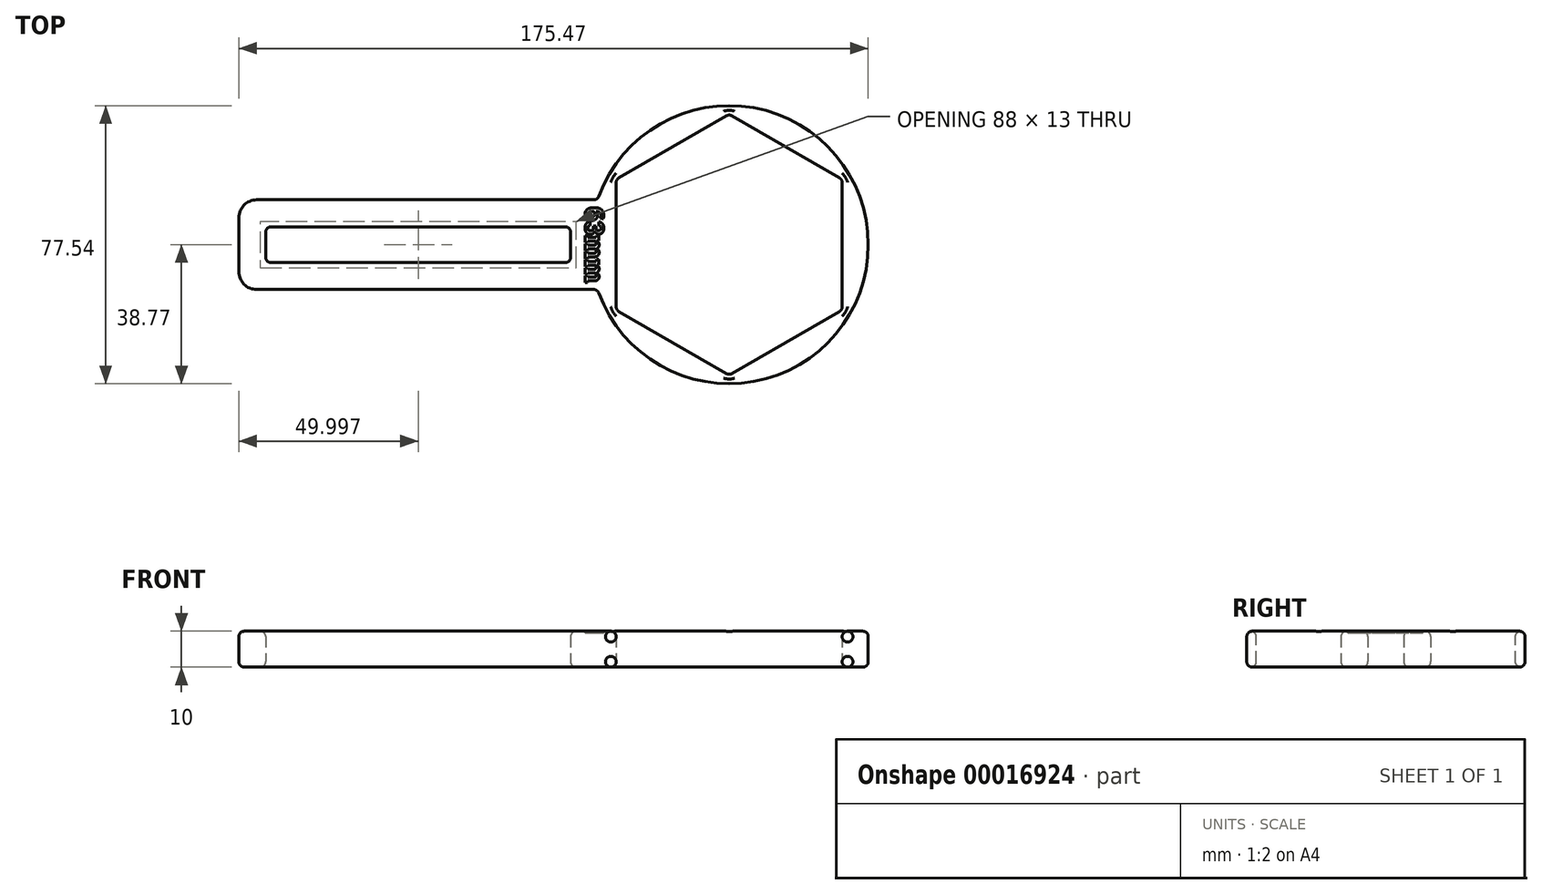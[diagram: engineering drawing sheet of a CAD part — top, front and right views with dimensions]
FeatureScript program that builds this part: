
annotation { "Feature Type Name" : "Feature", "Feature Type Description" : "" }
export const myFeature = defineFeature(function(context is Context, id is Id, definition is map)
    precondition{}
    {
        {
            var Q0;
            Q0=qCreatedBy(makeId("Top.planeOp"),FACE);
            var sketch = newSketch(context, id + "F0", { "sketchPlane" : qUnion([Q0])});
            skCircle(sketch, "E0.cCircle", {"center": v(0, 0) * mm, "radius": 31.5 * mm, "construction": true});
            skLineSegment(sketch, "E0.0", {"start": v(31.5, 18.19) * mm, "end": v(31.5, -18.19) * mm});
            skLineSegment(sketch, "E0.1", {"start": v(31.5, -18.19) * mm, "end": v(0, -36.37) * mm});
            skLineSegment(sketch, "E0.2", {"start": v(0, -36.37) * mm, "end": v(-31.5, -18.19) * mm});
            skLineSegment(sketch, "E0.3", {"start": v(-31.5, -18.19) * mm, "end": v(-31.5, 18.19) * mm});
            skLineSegment(sketch, "E0.4", {"start": v(-31.5, 18.19) * mm, "end": v(0, 36.37) * mm});
            skLineSegment(sketch, "E0.5", {"start": v(0, 36.37) * mm, "end": v(31.5, 18.19) * mm});
            skPoint(sketch, "E0.0.midPoint", {"position": v(31.5, 0) * mm});
            skArc(sketch, "E1", {"start": v(-36.7, -12.5) * mm, "mid": v(38.77, 0) * mm, "end": v(-36.7, 12.5) * mm});
            skLineSegment(sketch, "E2.rect.bottom", {"start": v(-36.7, 12.5) * mm, "end": v(-136.7, 12.5) * mm});
            skLineSegment(sketch, "E2.rect.top", {"start": v(-36.7, -12.5) * mm, "end": v(-136.7, -12.5) * mm});
            skLineSegment(sketch, "E2.rect.left", {"start": v(-31.5, 12.5) * mm, "end": v(-31.5, -12.5) * mm});
            skLineSegment(sketch, "E2.rect.right", {"start": v(-136.7, 12.5) * mm, "end": v(-136.7, -12.5) * mm});
            skPoint(sketch, "E2.rect.middle", {"position": v(-84.1, 0) * mm});
            skLineSegment(sketch, "E3.rect.bottom", {"start": v(-44.2, 5) * mm, "end": v(-129.2, 5) * mm});
            skLineSegment(sketch, "E3.rect.top", {"start": v(-44.2, -5) * mm, "end": v(-129.2, -5) * mm});
            skLineSegment(sketch, "E3.rect.left", {"start": v(-44.2, 5) * mm, "end": v(-44.2, -5) * mm});
            skLineSegment(sketch, "E3.rect.right", {"start": v(-129.2, 5) * mm, "end": v(-129.2, -5) * mm});
            skPoint(sketch, "E3.rect.middle", {"position": v(-86.7, 0) * mm});
            skSolve(sketch);
        }
        {
            var Q0;
            Q0=makeQuery(id+"F0.imprint","IMPRINT",FACE,{"disambiguationData":[TD([[makeQuery(id+"F0.imprint","IMPRINT",EDGE,{"derivedFrom":sQuery(id+"F0.wireOp",EDGE,"E0.0")}),1.0]])]});
            extrude(context, id + "F1", {"entities" : qUnion([Q0]), "depth" : 10 * mm});
        }
        {
            var Q0;
            Q0=makeQuery(id+"F1.opExtrude","CAP_EDGE",EDGE,{"disambiguationData":[OSD([sQuery(id+"F0.wireOp",EDGE,"E3.rect.right")])],"isStart":false});
            var Q1;
            Q1=makeQuery(id+"F1.opExtrude","CAP_EDGE",EDGE,{"disambiguationData":[OSD([sQuery(id+"F0.wireOp",EDGE,"E2.rect.right")])],"isStart":false});
            var Q2;
            Q2=makeQuery(id+"F1.opExtrude","SWEPT_EDGE",EDGE,{"disambiguationData":[OSD([sQuery(id+"F0.wireOp",EDGE,"E3.rect.bottom"),sQuery(id+"F0.wireOp",EDGE,"E3.rect.right")])]});
            var Q3;
            Q3=makeQuery(id+"F1.opExtrude","CAP_EDGE",EDGE,{"disambiguationData":[OSD([sQuery(id+"F0.wireOp",EDGE,"E2.rect.right")])],"isStart":true});
            var Q4;
            Q4=makeQuery(id+"F1.opExtrude","CAP_EDGE",EDGE,{"disambiguationData":[OSD([sQuery(id+"F0.wireOp",EDGE,"E3.rect.right")])],"isStart":true});
            var Q5;
            Q5=makeQuery(id+"F1.opExtrude","SWEPT_EDGE",EDGE,{"disambiguationData":[OSD([sQuery(id+"F0.wireOp",EDGE,"E3.rect.top"),sQuery(id+"F0.wireOp",EDGE,"E3.rect.right")])]});
            var Q6;
            Q6=makeQuery(id+"F1.opExtrude","CAP_EDGE",EDGE,{"disambiguationData":[OSD([sQuery(id+"F0.wireOp",EDGE,"E3.rect.bottom")])],"isStart":false});
            var Q7;
            Q7=makeQuery(id+"F1.opExtrude","CAP_EDGE",EDGE,{"disambiguationData":[OSD([sQuery(id+"F0.wireOp",EDGE,"E3.rect.bottom")])],"isStart":true});
            var Q8;
            Q8=makeQuery(id+"F1.opExtrude","CAP_EDGE",EDGE,{"disambiguationData":[OSD([sQuery(id+"F0.wireOp",EDGE,"E2.rect.top")])],"isStart":false});
            var Q9;
            Q9=makeQuery(id+"F1.opExtrude","CAP_EDGE",EDGE,{"disambiguationData":[OSD([sQuery(id+"F0.wireOp",EDGE,"E3.rect.top")])],"isStart":false});
            var Q10;
            Q10=makeQuery(id+"F1.opExtrude","CAP_EDGE",EDGE,{"disambiguationData":[OSD([sQuery(id+"F0.wireOp",EDGE,"E2.rect.top")])],"isStart":true});
            var Q11;
            Q11=makeQuery(id+"F1.opExtrude","CAP_EDGE",EDGE,{"disambiguationData":[OSD([sQuery(id+"F0.wireOp",EDGE,"E2.rect.bottom")])],"isStart":false});
            var Q12;
            Q12=makeQuery(id+"F1.opExtrude","CAP_EDGE",EDGE,{"disambiguationData":[OSD([sQuery(id+"F0.wireOp",EDGE,"E2.rect.bottom")])],"isStart":true});
            var Q13;
            Q13=makeQuery(id+"F1.opExtrude","CAP_EDGE",EDGE,{"disambiguationData":[OSD([sQuery(id+"F0.wireOp",EDGE,"E3.rect.top")])],"isStart":true});
            var Q14;
            Q14=makeQuery(id+"F1.opExtrude","CAP_EDGE",EDGE,{"disambiguationData":[OSD([sQuery(id+"F0.wireOp",EDGE,"E0.2")])],"isStart":false});
            var Q15;
            Q15=makeQuery(id+"F1.opExtrude","CAP_EDGE",EDGE,{"disambiguationData":[OSD([sQuery(id+"F0.wireOp",EDGE,"E1")])],"isStart":true});
            var Q16;
            Q16=makeQuery(id+"F1.opExtrude","CAP_EDGE",EDGE,{"disambiguationData":[OSD([sQuery(id+"F0.wireOp",EDGE,"E0.1")])],"isStart":false});
            var Q17;
            Q17=makeQuery(id+"F1.opExtrude","SWEPT_EDGE",EDGE,{"disambiguationData":[OSD([sQuery(id+"F0.wireOp",EDGE,"E1"),sQuery(id+"F0.wireOp",EDGE,"E2.rect.top")])]});
            var Q18;
            Q18=makeQuery(id+"F1.opExtrude","CAP_EDGE",EDGE,{"disambiguationData":[OSD([sQuery(id+"F0.wireOp",EDGE,"E0.0")])],"isStart":false});
            var Q19;
            Q19=makeQuery(id+"F1.opExtrude","CAP_EDGE",EDGE,{"disambiguationData":[OSD([sQuery(id+"F0.wireOp",EDGE,"E0.3"),sQuery(id+"F0.wireOp",EDGE,"E2.rect.left")])],"isStart":false});
            var Q20;
            Q20=makeQuery(id+"F1.opExtrude","CAP_EDGE",EDGE,{"disambiguationData":[OSD([sQuery(id+"F0.wireOp",EDGE,"E1")])],"isStart":false});
            var Q21;
            Q21=makeQuery(id+"F1.opExtrude","CAP_EDGE",EDGE,{"disambiguationData":[OSD([sQuery(id+"F0.wireOp",EDGE,"E0.2")])],"isStart":true});
            var Q22;
            Q22=makeQuery(id+"F1.opExtrude","CAP_EDGE",EDGE,{"disambiguationData":[OSD([sQuery(id+"F0.wireOp",EDGE,"E0.5")])],"isStart":false});
            var Q23;
            Q23=makeQuery(id+"F1.opExtrude","SWEPT_EDGE",EDGE,{"disambiguationData":[OSD([sQuery(id+"F0.wireOp",EDGE,"E3.rect.top"),sQuery(id+"F0.wireOp",EDGE,"E3.rect.left")])]});
            var Q24;
            Q24=makeQuery(id+"F1.opExtrude","SWEPT_EDGE",EDGE,{"disambiguationData":[OSD([sQuery(id+"F0.wireOp",EDGE,"E3.rect.bottom"),sQuery(id+"F0.wireOp",EDGE,"E3.rect.left")])]});
            var Q25;
            Q25=makeQuery(id+"F1.opExtrude","SWEPT_EDGE",EDGE,{"disambiguationData":[OSD([sQuery(id+"F0.wireOp",EDGE,"E1"),sQuery(id+"F0.wireOp",EDGE,"E2.rect.bottom")])]});
            var Q26;
            Q26=makeQuery(id+"F1.opExtrude","SWEPT_EDGE",EDGE,{"disambiguationData":[OSD([sQuery(id+"F0.wireOp",EDGE,"E0.4"),sQuery(id+"F0.wireOp",EDGE,"E0.5")])]});
            var Q27;
            Q27=makeQuery(id+"F1.opExtrude","SWEPT_EDGE",EDGE,{"disambiguationData":[OSD([sQuery(id+"F0.wireOp",EDGE,"E0.3"),sQuery(id+"F0.wireOp",EDGE,"E0.4")])]});
            var Q28;
            Q28=makeQuery(id+"F1.opExtrude","CAP_EDGE",EDGE,{"disambiguationData":[OSD([sQuery(id+"F0.wireOp",EDGE,"E0.5")])],"isStart":true});
            var Q29;
            Q29=makeQuery(id+"F1.opExtrude","SWEPT_EDGE",EDGE,{"disambiguationData":[OSD([sQuery(id+"F0.wireOp",EDGE,"E0.2"),sQuery(id+"F0.wireOp",EDGE,"E0.3")])]});
            var Q30;
            Q30=makeQuery(id+"F1.opExtrude","SWEPT_EDGE",EDGE,{"disambiguationData":[OSD([sQuery(id+"F0.wireOp",EDGE,"E0.1"),sQuery(id+"F0.wireOp",EDGE,"E0.2")])]});
            var Q31;
            Q31=makeQuery(id+"F1.opExtrude","SWEPT_EDGE",EDGE,{"disambiguationData":[OSD([sQuery(id+"F0.wireOp",EDGE,"E0.0"),sQuery(id+"F0.wireOp",EDGE,"E0.1")])]});
            var Q32;
            Q32=makeQuery(id+"F1.opExtrude","SWEPT_EDGE",EDGE,{"disambiguationData":[OSD([sQuery(id+"F0.wireOp",EDGE,"E0.0"),sQuery(id+"F0.wireOp",EDGE,"E0.5")])]});
            var Q33;
            Q33=makeQuery(id+"F1.opExtrude","CAP_EDGE",EDGE,{"disambiguationData":[OSD([sQuery(id+"F0.wireOp",EDGE,"E0.0")])],"isStart":true});
            var Q34;
            Q34=makeQuery(id+"F1.opExtrude","CAP_EDGE",EDGE,{"disambiguationData":[OSD([sQuery(id+"F0.wireOp",EDGE,"E0.1")])],"isStart":true});
            var Q35;
            Q35=makeQuery(id+"F1.opExtrude","CAP_EDGE",EDGE,{"disambiguationData":[OSD([sQuery(id+"F0.wireOp",EDGE,"E3.rect.left")])],"isStart":false});
            var Q36;
            Q36=makeQuery(id+"F1.opExtrude","CAP_EDGE",EDGE,{"disambiguationData":[OSD([sQuery(id+"F0.wireOp",EDGE,"E0.4")])],"isStart":false});
            var Q37;
            Q37=makeQuery(id+"F1.opExtrude","CAP_EDGE",EDGE,{"disambiguationData":[OSD([sQuery(id+"F0.wireOp",EDGE,"E0.4")])],"isStart":true});
            var Q38;
            Q38=makeQuery(id+"F1.opExtrude","CAP_EDGE",EDGE,{"disambiguationData":[OSD([sQuery(id+"F0.wireOp",EDGE,"E0.3"),sQuery(id+"F0.wireOp",EDGE,"E2.rect.left")])],"isStart":true});
            var Q39;
            Q39=makeQuery(id+"F1.opExtrude","CAP_EDGE",EDGE,{"disambiguationData":[OSD([sQuery(id+"F0.wireOp",EDGE,"E3.rect.left")])],"isStart":true});
            fillet(context, id + "F2", {"entities" : qUnion([Q0, Q1, Q2, Q3, Q4, Q5, Q6, Q7, Q8, Q9, Q10, Q11, Q12, Q13, Q14, Q15, Q16, Q17, Q18, Q19, Q20, Q21, Q22, Q23, Q24, Q25, Q26, Q27, Q28, Q29, Q30, Q31, Q32, Q33, Q34, Q35, Q36, Q37, Q38, Q39]), "radius" : 1.5 * mm, "tangentPropagation" : true, "allowEdgeOverflow" : false});
        }
        {
            var Q0;
            Q0=makeQuery(id+"F1.opExtrude","SWEPT_EDGE",EDGE,{"disambiguationData":[OSD([sQuery(id+"F0.wireOp",EDGE,"E2.rect.top"),sQuery(id+"F0.wireOp",EDGE,"E2.rect.right")])]});
            var Q1;
            Q1=makeQuery(id+"F1.opExtrude","SWEPT_EDGE",EDGE,{"disambiguationData":[OSD([sQuery(id+"F0.wireOp",EDGE,"E2.rect.bottom"),sQuery(id+"F0.wireOp",EDGE,"E2.rect.right")])]});
            fillet(context, id + "F3", {"entities" : qUnion([Q0, Q1]), "radius" : 5 * mm, "tangentPropagation" : true, "allowEdgeOverflow" : false});
        }
        {
            var Q0;
            Q0=makeQuery(id+"F2.opFillet","SPLIT",FACE,{"disambiguationData":[OD(0.0)],"derivedFrom":makeQuery(id+"F1.opExtrude","CAP_FACE",FACE,{"disambiguationData":[OSD([sQuery(id+"F0.wireOp",EDGE,"E0.0"),sQuery(id+"F0.wireOp",EDGE,"E0.1"),sQuery(id+"F0.wireOp",EDGE,"E0.2"),sQuery(id+"F0.wireOp",EDGE,"E0.3"),sQuery(id+"F0.wireOp",EDGE,"E0.4"),sQuery(id+"F0.wireOp",EDGE,"E0.5"),sQuery(id+"F0.wireOp",EDGE,"E1"),sQuery(id+"F0.wireOp",EDGE,"E2.rect.bottom"),sQuery(id+"F0.wireOp",EDGE,"E2.rect.top"),sQuery(id+"F0.wireOp",EDGE,"E2.rect.left"),sQuery(id+"F0.wireOp",EDGE,"E2.rect.right"),sQuery(id+"F0.wireOp",EDGE,"E3.rect.bottom"),sQuery(id+"F0.wireOp",EDGE,"E3.rect.top"),sQuery(id+"F0.wireOp",EDGE,"E3.rect.left"),sQuery(id+"F0.wireOp",EDGE,"E3.rect.right")])],"isStart":false})});
            var sketch = newSketch(context, id + "F4", { "sketchPlane" : qUnion([Q0])});
            skText(sketch, "E4", { "text": "63mm", "fontName": "RobotoSlab-Bold.ttf"});
            skLineSegment(sketch, "E5", {"start": v(0, 0) * mm, "end": v(-56.58, 0) * mm, "construction": true});
            skLineSegment(sketch, "E6", {"start": v(-34.95, 12.96) * mm, "end": v(-34.95, -12.96) * mm, "construction": true});
            const initialGuessF4  = {"E4": [-0.04013, 0.0106, 0, -1, 0.00518]};
            skSetInitialGuess(sketch, initialGuessF4);
            skSolve(sketch);
        }
        {
            var Q0;
            Q0 = qSketchRegion(id + "F4", true);
            extrude(context, id + "F5", {"entities" : qUnion([Q0]), "operationType" : NewBodyOperationType.REMOVE, "oppositeDirection" : true, "depth" : 0.5 * mm});
        }
    });
